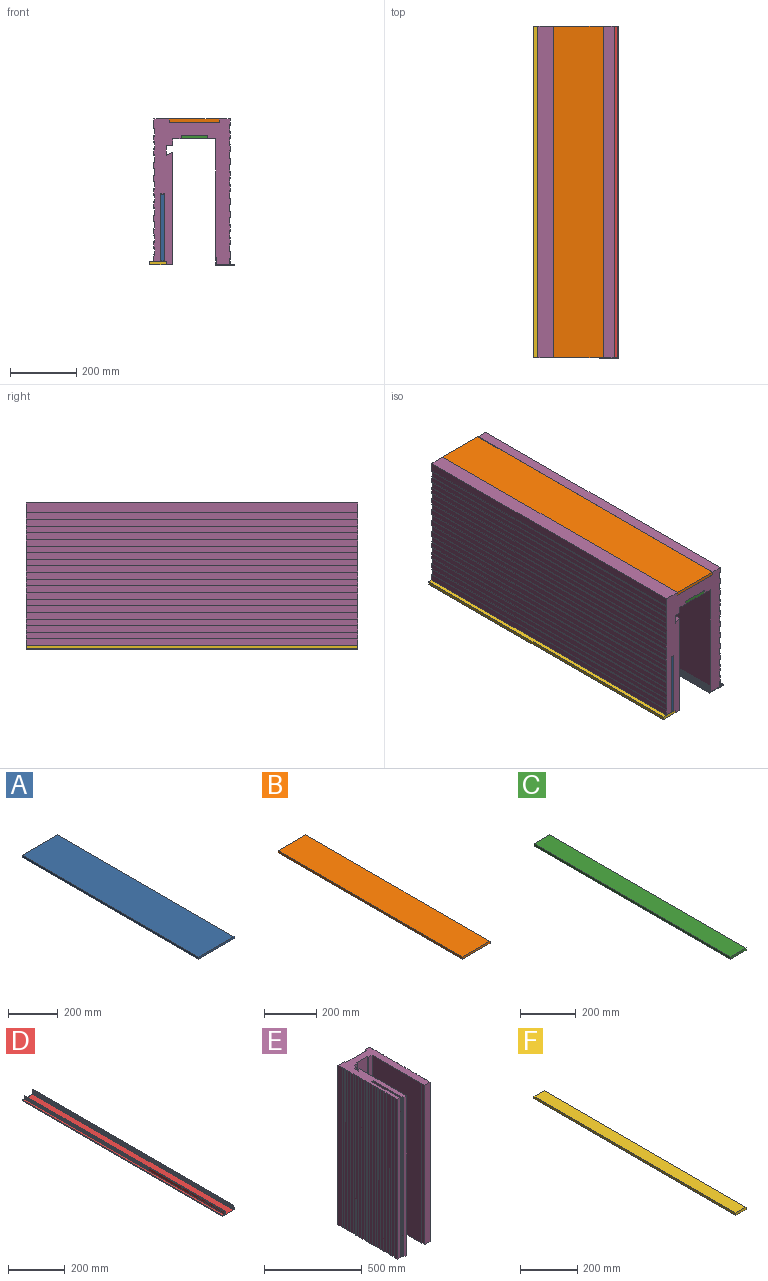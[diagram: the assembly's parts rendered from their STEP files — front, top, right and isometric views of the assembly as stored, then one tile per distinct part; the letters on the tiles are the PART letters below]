
ASSEMBLY  parts=6 mates=5
PART A: 6 faces, bbox 200x1000x10 mm
  f0: plane 1000x10mm, normal (-1,0,0), area 10000mm2, adj f1,f3,f4,f5
  f1: plane 1000x200mm, normal (0,0,-1), area 200000mm2, adj f0,f2,f4,f5
  f2: plane 1000x10mm, normal (1,0,0), area 10000mm2, adj f1,f3,f4,f5
  f3: plane 1000x200mm, normal (0,0,1), area 200000mm2, adj f0,f2,f4,f5
  f4: plane 200x10mm, normal (0,-1,0), area 2000mm2, adj f0,f1,f2,f3
  f5: plane 200x10mm, normal (0,1,0), area 2000mm2, adj f0,f1,f2,f3
PART B: 6 faces, bbox 150x1000x10 mm
  f0: plane 1000x10mm, normal (-1,0,0), area 10000mm2, adj f1,f3,f4,f5
  f1: plane 1000x150mm, normal (0,0,-1), area 150000mm2, adj f0,f2,f4,f5
  f2: plane 1000x10mm, normal (1,0,0), area 10000mm2, adj f1,f3,f4,f5
  f3: plane 1000x150mm, normal (0,0,1), area 150000mm2, adj f0,f2,f4,f5
  f4: plane 150x10mm, normal (0,-1,0), area 1500mm2, adj f0,f1,f2,f3
  f5: plane 150x10mm, normal (0,1,0), area 1500mm2, adj f0,f1,f2,f3
PART C: 6 faces, bbox 80x1000x10 mm
  f0: plane 1000x10mm, normal (-1,0,0), area 10000mm2, adj f1,f3,f4,f5
  f1: plane 1000x80mm, normal (0,0,-1), area 80000mm2, adj f0,f2,f4,f5
  f2: plane 1000x10mm, normal (1,0,0), area 10000mm2, adj f1,f3,f4,f5
  f3: plane 1000x80mm, normal (0,0,1), area 80000mm2, adj f0,f2,f4,f5
  f4: plane 80x10mm, normal (0,-1,0), area 800mm2, adj f0,f1,f2,f3
  f5: plane 80x10mm, normal (0,1,0), area 800mm2, adj f0,f1,f2,f3
PART D: 62 faces, bbox 57.5x1000x21 mm
  f0: plane 1000x14.3mm, normal (-1,0,0), area 14303.9mm2, adj f1,f2,f60,f61
  f1: plane 57.5x21mm, normal (0,-1,0), area 145.8mm2, adj f0,f2,f3,f4,f5,f6,f7,f8
  f2: plane 1000x11mm, normal (0,0,1), area 11000mm2, adj f0,f1,f3,f60
  f3: plane 1000x1.5mm, normal (1,0,0), area 1500mm2, adj f1,f2,f4,f60
  f4: plane 1000x1.5mm, normal (0,0,1), area 1500mm2, adj f1,f3,f5,f60
  f5: plane 1000x3mm, normal (-1,0,0), area 3000mm2, adj f1,f4,f6,f60
  f6: plane 1000x57.5mm, normal (0,0,-1), area 57500mm2, adj f1,f5,f7,f60
  f7: plane 1000x4mm, normal (1,0,0), area 4000mm2, adj f1,f6,f8,f60
  f8: plane 1000x1mm, normal (0,0,1), area 1000mm2, adj f1,f7,f9,f60
  f9: plane 1000x3mm, normal (-1,0,0), area 3000mm2, adj f1,f8,f10,f60
  f10: plane 1000x1mm, normal (0,0,1), area 1000mm2, adj f1,f9,f11,f60
  f11: plane 1000x7mm, normal (1,0,0), area 7000mm2, adj f1,f10,f12,f60
  f12: plane 1000x1mm, normal (0,0,-1), area 1000mm2, adj f1,f11,f13,f60
  f13: plane 1000x3mm, normal (-1,0,0), area 3000mm2, adj f1,f12,f14,f60
  f14: plane 1000x1mm, normal (0,0,-1), area 1000mm2, adj f1,f13,f15,f60
  f15: plane 1000x4mm, normal (1,0,0), area 4000mm2, adj f1,f14,f16,f60
  f16: plane 1000x2mm, normal (0,0,1), area 2000mm2, adj f1,f15,f17,f60
  f17: plane 1000x12mm, normal (1,0,0), area 12000mm2, adj f1,f16,f18,f60
  f18: plane 1000x1mm, normal (0,0,1), area 1000mm2, adj f1,f17,f19,f60
  f19: plane 1000x1.73mm, normal (-0.87,0,0.5), area 2000mm2, adj f1,f18,f20,f60
  f20: plane 1000x1mm, normal (0,0,-1), area 1000mm2, adj f1,f19,f21,f60
  f21: plane 1000x1.73mm, normal (-0.87,0,0.5), area 2000mm2, adj f1,f20,f22,f60
  f22: plane 1000x1mm, normal (0,0,-1), area 1000mm2, adj f1,f21,f23,f60
  f23: plane 1000x1.73mm, normal (-0.87,0,0.5), area 2000mm2, adj f1,f22,f24,f60
  f24: plane 1000x1mm, normal (0,0,-1), area 1000mm2, adj f1,f23,f25,f60
  f25: plane 1000x1.73mm, normal (-0.87,0,0.5), area 2000mm2, adj f1,f24,f26,f60
  f26: plane 1000x1mm, normal (0,0,-1), area 1000mm2, adj f1,f25,f27,f60
  f27: plane 1000x1.73mm, normal (-0.87,0,0.5), area 2000mm2, adj f1,f26,f28,f60
  f28: plane 1000x1mm, normal (0,0,-1), area 1000mm2, adj f1,f27,f29,f60
  f29: plane 1000x1.73mm, normal (-0.87,0,0.5), area 2000mm2, adj f1,f28,f30,f60
  f30: plane 1000x1mm, normal (0,0,-1), area 1000mm2, adj f1,f29,f31,f60
  f31: plane 1000x1.73mm, normal (-0.87,0,0.5), area 2000mm2, adj f1,f30,f32,f60
  f32: plane 1000x1mm, normal (0,0,-1), area 1000mm2, adj f1,f31,f33,f60
  f33: plane 1000x1.73mm, normal (-0.87,0,0.5), area 2000mm2, adj f1,f32,f34,f60
  f34: plane 1000x1mm, normal (0,0,-1), area 1000mm2, adj f1,f33,f35,f60
  f35: plane 1000x1.73mm, normal (-0.87,0,0.5), area 2000mm2, adj f1,f34,f36,f60
  f36: plane 1000x1mm, normal (0,0,-1), area 1000mm2, adj f1,f35,f37,f60
  f37: plane 1000x1.73mm, normal (-0.87,0,0.5), area 2000mm2, adj f1,f36,f38,f60
  f38: plane 1000x1mm, normal (0,0,-1), area 1000mm2, adj f1,f37,f39,f60
  f39: plane 1000x1.73mm, normal (-0.87,0,0.5), area 2000mm2, adj f1,f38,f40,f60
  f40: plane 1000x1mm, normal (0,0,-1), area 1000mm2, adj f1,f39,f41,f60
  f41: plane 1000x0.45mm, normal (-1,0,0), area 447.4mm2, adj f1,f40,f42,f60
  f42: plane 1000x41mm, normal (0,0,1), area 41000mm2, adj f1,f41,f43,f60
  f43: plane 1000x0.45mm, normal (1,0,0), area 447.4mm2, adj f1,f42,f44,f60
  f44: plane 1000x1mm, normal (0,0,-1), area 1000mm2, adj f1,f43,f45,f60
  f45: plane 1000x1.73mm, normal (0.87,0,0.5), area 2000mm2, adj f1,f44,f46,f60
  f46: plane 1000x1mm, normal (0,0,-1), area 1000mm2, adj f1,f45,f47,f60
  f47: plane 1000x1.73mm, normal (0.87,0,0.5), area 2000mm2, adj f1,f46,f48,f60
  f48: plane 1000x1mm, normal (0,0,-1), area 1000mm2, adj f1,f47,f49,f60
  f49: plane 1000x1.73mm, normal (0.87,0,0.5), area 2000mm2, adj f1,f48,f50,f60
  f50: plane 1000x1mm, normal (0,0,-1), area 1000mm2, adj f1,f49,f51,f60
  f51: plane 1000x1.73mm, normal (0.87,0,0.5), area 2000mm2, adj f1,f50,f52,f60
  f52: plane 1000x1mm, normal (0,0,-1), area 1000mm2, adj f1,f51,f53,f60
  f53: plane 1000x1.73mm, normal (0.87,0,0.5), area 2000mm2, adj f1,f52,f54,f60
  f54: plane 1000x1mm, normal (0,0,-1), area 1000mm2, adj f1,f53,f55,f60
  f55: plane 1000x1.73mm, normal (0.87,0,0.5), area 2000mm2, adj f1,f54,f56,f60
  f56: plane 1000x1mm, normal (0,0,-1), area 1000mm2, adj f1,f55,f57,f60
  f57: plane 1000x1.73mm, normal (0.87,0,0.5), area 2000mm2, adj f1,f56,f58,f60
  f58: plane 1000x1mm, normal (0,0,-1), area 1000mm2, adj f1,f57,f59,f60
  f59: plane 1000x1.73mm, normal (0.87,0,0.5), area 2000mm2, adj f1,f58,f60,f61
  f60: plane 57.5x21mm, normal (0,1,0), area 145.8mm2, adj f0,f2,f3,f4,f5,f6,f7,f8
  f61: plane 1000x1mm, normal (0,0,1), area 1000mm2, adj f0,f1,f59,f60
PART E: 112 faces, bbox 230x440x1000 mm
  f0: plane 1000x20mm, normal (-1,0,0), area 20000mm2, adj f50,f51,f106,f110
  f1: plane 1000x20mm, normal (-1,0,0), area 20000mm2, adj f50,f51,f103,f107
  f2: plane 1000x20mm, normal (-1,0,0), area 20000mm2, adj f50,f51,f100,f104
  f3: plane 1000x20mm, normal (-1,0,0), area 20000mm2, adj f50,f51,f97,f101
  f4: plane 1000x20mm, normal (-1,0,0), area 20000mm2, adj f50,f51,f94,f98
  f5: plane 1000x20mm, normal (-1,0,0), area 20000mm2, adj f50,f51,f91,f95
  f6: plane 1000x20mm, normal (-1,0,0), area 20000mm2, adj f50,f51,f88,f92
  f7: plane 1000x20mm, normal (-1,0,0), area 20000mm2, adj f50,f51,f85,f89
  f8: plane 1000x20mm, normal (-1,0,0), area 20000mm2, adj f50,f51,f82,f86
  f9: plane 1000x30mm, normal (-1,0,0), area 30000mm2, adj f21,f50,f51,f83
  f10: plane 1000x22mm, normal (1,0,0), area 22000mm2, adj f45,f50,f51,f79
  f11: plane 1000x20mm, normal (1,0,0), area 20000mm2, adj f50,f51,f76,f80
  f12: plane 1000x20mm, normal (1,0,0), area 20000mm2, adj f50,f51,f73,f77
  f13: plane 1000x20mm, normal (1,0,0), area 20000mm2, adj f50,f51,f70,f74
  f14: plane 1000x20mm, normal (1,0,0), area 20000mm2, adj f50,f51,f67,f71
  f15: plane 1000x20mm, normal (1,0,0), area 20000mm2, adj f50,f51,f64,f68
  f16: plane 1000x20mm, normal (1,0,0), area 20000mm2, adj f50,f51,f61,f65
  f17: plane 1000x20mm, normal (1,0,0), area 20000mm2, adj f50,f51,f58,f62
  f18: plane 1000x20mm, normal (1,0,0), area 20000mm2, adj f50,f51,f55,f59
  f19: plane 1000x20mm, normal (1,0,0), area 20000mm2, adj f50,f51,f52,f56
  f20: plane 1000x10mm, normal (1,0,0), area 10000mm2, adj f21,f49,f50,f51
  f21: plane 1000x46.75mm, normal (0,1,0), area 46750mm2, adj f9,f20,f50,f51
  f22: plane 1000x20mm, normal (-1,0,0), area 20000mm2, adj f23,f50,f51,f109
  f23: plane 1000x20.5mm, normal (0,-1,0), area 20500mm2, adj f22,f24,f50,f51
  f24: plane 1000x205mm, normal (1,0,0), area 205000mm2, adj f23,f25,f50,f51
  f25: cylinder r=10mm len=1000mm, axis (0,0,-1), area 11054.3mm2, adj f24,f26,f50,f51
  f26: plane 1000x205mm, normal (-1,0,0), area 205000mm2, adj f25,f27,f50,f51
  f27: plane 1000x6mm, normal (0,-1,0), area 6000mm2, adj f26,f28,f50,f51
  f28: plane 1000x10mm, normal (-1,0,0), area 10000mm2, adj f27,f29,f50,f51
  f29: plane 1000x20mm, normal (0,-1,0), area 20000mm2, adj f28,f30,f50,f51
  f30: plane 1000x340.19mm, normal (1,0,0), area 340190.5mm2, adj f29,f31,f50,f51
  f31: plane 1000x20mm, normal (-0.45,0.89,0), area 22446.5mm2, adj f30,f32,f50,f51
  f32: plane 1000x30mm, normal (1,0,0), area 30000mm2, adj f31,f33,f50,f51
  f33: plane 1000x20mm, normal (0,-1,0), area 20000mm2, adj f32,f34,f50,f51
  f34: plane 1000x20mm, normal (1,0,0), area 20000mm2, adj f33,f35,f50,f51
  f35: plane 1000x24.75mm, normal (0,-1,0), area 24750mm2, adj f34,f36,f50,f51
  f36: plane 1000x10mm, normal (1,0,0), area 10000mm2, adj f35,f37,f50,f51
  f37: plane 1000x80.5mm, normal (0,-1,0), area 80500mm2, adj f36,f38,f50,f51
  f38: plane 1000x10mm, normal (-1,0,0), area 10000mm2, adj f37,f39,f50,f51
  f39: plane 1000x24.75mm, normal (0,-1,0), area 24750mm2, adj f38,f40,f50,f51
  f40: plane 1000x357.5mm, normal (-1,0,0), area 357500mm2, adj f39,f41,f50,f51
  f41: plane 1000x2mm, normal (0,-1,0), area 2000mm2, adj f40,f42,f50,f51
  f42: plane 1000x21.5mm, normal (-1,0,0), area 21500mm2, adj f41,f43,f50,f51
  f43: plane 1000x39.1mm, normal (0,-1,0), area 39100mm2, adj f42,f44,f50,f51
  f44: plane 1000x18.5mm, normal (1,0,0), area 18500mm2, adj f43,f45,f50,f51
  f45: plane 1000x1.9mm, normal (0,-1,0), area 1900mm2, adj f10,f44,f50,f51
  f46: plane 1000x18.5mm, normal (1,0,0), area 18500mm2, adj f47,f50,f51,f53
  f47: plane 1000x32.75mm, normal (0,1,0), area 32750mm2, adj f46,f48,f50,f51
  f48: plane 1000x10mm, normal (-1,0,0), area 10000mm2, adj f47,f49,f50,f51
  f49: plane 1000x150.5mm, normal (0,1,0), area 150500mm2, adj f20,f48,f50,f51
  f50: plane 440x230mm, normal (0,0,1), area 45478.8mm2, adj f0,f1,f2,f3,f4,f5,f6,f7
  f51: plane 440x230mm, normal (0,0,-1), area 45478.8mm2, adj f0,f1,f2,f3,f4,f5,f6,f7
  f52: plane 1000x2mm, normal (-0.71,0.71,0), area 2828.4mm2, adj f19,f50,f51,f54
  f53: plane 1000x2mm, normal (-0.71,-0.71,0), area 2828.4mm2, adj f46,f50,f51,f54
  f54: plane 1000x24mm, normal (1,0,0), area 24000mm2, adj f50,f51,f52,f53
  f55: plane 1000x2mm, normal (-0.71,0.71,0), area 2828.4mm2, adj f18,f50,f51,f57
  f56: plane 1000x2mm, normal (-0.71,-0.71,0), area 2828.4mm2, adj f19,f50,f51,f57
  f57: plane 1000x24mm, normal (1,0,0), area 24000mm2, adj f50,f51,f55,f56
  f58: plane 1000x2mm, normal (-0.71,0.71,0), area 2828.4mm2, adj f17,f50,f51,f60
  f59: plane 1000x2mm, normal (-0.71,-0.71,0), area 2828.4mm2, adj f18,f50,f51,f60
  f60: plane 1000x24mm, normal (1,0,0), area 24000mm2, adj f50,f51,f58,f59
  f61: plane 1000x2mm, normal (-0.71,0.71,0), area 2828.4mm2, adj f16,f50,f51,f63
  f62: plane 1000x2mm, normal (-0.71,-0.71,0), area 2828.4mm2, adj f17,f50,f51,f63
  f63: plane 1000x24mm, normal (1,0,0), area 24000mm2, adj f50,f51,f61,f62
  f64: plane 1000x2mm, normal (-0.71,0.71,0), area 2828.4mm2, adj f15,f50,f51,f66
  f65: plane 1000x2mm, normal (-0.71,-0.71,0), area 2828.4mm2, adj f16,f50,f51,f66
  f66: plane 1000x24mm, normal (1,0,0), area 24000mm2, adj f50,f51,f64,f65
  f67: plane 1000x2mm, normal (-0.71,0.71,0), area 2828.4mm2, adj f14,f50,f51,f69
  f68: plane 1000x2mm, normal (-0.71,-0.71,0), area 2828.4mm2, adj f15,f50,f51,f69
  f69: plane 1000x24mm, normal (1,0,0), area 24000mm2, adj f50,f51,f67,f68
  f70: plane 1000x2mm, normal (-0.71,0.71,0), area 2828.4mm2, adj f13,f50,f51,f72
  f71: plane 1000x2mm, normal (-0.71,-0.71,0), area 2828.4mm2, adj f14,f50,f51,f72
  f72: plane 1000x24mm, normal (1,0,0), area 24000mm2, adj f50,f51,f70,f71
  f73: plane 1000x2mm, normal (-0.71,0.71,0), area 2828.4mm2, adj f12,f50,f51,f75
  f74: plane 1000x2mm, normal (-0.71,-0.71,0), area 2828.4mm2, adj f13,f50,f51,f75
  f75: plane 1000x24mm, normal (1,0,0), area 24000mm2, adj f50,f51,f73,f74
  f76: plane 1000x2mm, normal (-0.71,0.71,0), area 2828.4mm2, adj f11,f50,f51,f78
  f77: plane 1000x2mm, normal (-0.71,-0.71,0), area 2828.4mm2, adj f12,f50,f51,f78
  f78: plane 1000x24mm, normal (1,0,0), area 24000mm2, adj f50,f51,f76,f77
  f79: plane 1000x2mm, normal (-0.71,0.71,0), area 2828.4mm2, adj f10,f50,f51,f81
  f80: plane 1000x2mm, normal (-0.71,-0.71,0), area 2828.4mm2, adj f11,f50,f51,f81
  f81: plane 1000x24mm, normal (1,0,0), area 24000mm2, adj f50,f51,f79,f80
  f82: plane 1000x2mm, normal (0.71,0.71,0), area 2828.4mm2, adj f8,f50,f51,f84
  f83: plane 1000x2mm, normal (0.71,-0.71,0), area 2828.4mm2, adj f9,f50,f51,f84
  f84: plane 1000x24mm, normal (-1,0,0), area 24000mm2, adj f50,f51,f82,f83
  f85: plane 1000x2mm, normal (0.71,0.71,0), area 2828.4mm2, adj f7,f50,f51,f87
  f86: plane 1000x2mm, normal (0.71,-0.71,0), area 2828.4mm2, adj f8,f50,f51,f87
  f87: plane 1000x24mm, normal (-1,0,0), area 24000mm2, adj f50,f51,f85,f86
  f88: plane 1000x2mm, normal (0.71,0.71,0), area 2828.4mm2, adj f6,f50,f51,f90
  f89: plane 1000x2mm, normal (0.71,-0.71,0), area 2828.4mm2, adj f7,f50,f51,f90
  f90: plane 1000x24mm, normal (-1,0,0), area 24000mm2, adj f50,f51,f88,f89
  f91: plane 1000x2mm, normal (0.71,0.71,0), area 2828.4mm2, adj f5,f50,f51,f93
  f92: plane 1000x2mm, normal (0.71,-0.71,0), area 2828.4mm2, adj f6,f50,f51,f93
  f93: plane 1000x24mm, normal (-1,0,0), area 24000mm2, adj f50,f51,f91,f92
  f94: plane 1000x2mm, normal (0.71,0.71,0), area 2828.4mm2, adj f4,f50,f51,f96
  f95: plane 1000x2mm, normal (0.71,-0.71,0), area 2828.4mm2, adj f5,f50,f51,f96
  f96: plane 1000x24mm, normal (-1,0,0), area 24000mm2, adj f50,f51,f94,f95
  f97: plane 1000x2mm, normal (0.71,0.71,0), area 2828.4mm2, adj f3,f50,f51,f99
  f98: plane 1000x2mm, normal (0.71,-0.71,0), area 2828.4mm2, adj f4,f50,f51,f99
  f99: plane 1000x24mm, normal (-1,0,0), area 24000mm2, adj f50,f51,f97,f98
  f100: plane 1000x2mm, normal (0.71,0.71,0), area 2828.4mm2, adj f2,f50,f51,f102
  f101: plane 1000x2mm, normal (0.71,-0.71,0), area 2828.4mm2, adj f3,f50,f51,f102
  f102: plane 1000x24mm, normal (-1,0,0), area 24000mm2, adj f50,f51,f100,f101
  f103: plane 1000x2mm, normal (0.71,0.71,0), area 2828.4mm2, adj f1,f50,f51,f105
  f104: plane 1000x2mm, normal (0.71,-0.71,0), area 2828.4mm2, adj f2,f50,f51,f105
  f105: plane 1000x24mm, normal (-1,0,0), area 24000mm2, adj f50,f51,f103,f104
  f106: plane 1000x2mm, normal (0.71,0.71,0), area 2828.4mm2, adj f0,f50,f51,f108
  f107: plane 1000x2mm, normal (0.71,-0.71,0), area 2828.4mm2, adj f1,f50,f51,f108
  f108: plane 1000x24mm, normal (-1,0,0), area 24000mm2, adj f50,f51,f106,f107
  f109: plane 1000x2mm, normal (0.71,0.71,0), area 2828.4mm2, adj f22,f50,f51,f111
  f110: plane 1000x2mm, normal (0.71,-0.71,0), area 2828.4mm2, adj f0,f50,f51,f111
  f111: plane 1000x24mm, normal (-1,0,0), area 24000mm2, adj f50,f51,f109,f110
PART F: 6 faces, bbox 50x1000x10 mm
  f0: plane 1000x10mm, normal (-1,0,0), area 10000mm2, adj f1,f3,f4,f5
  f1: plane 1000x50mm, normal (0,0,-1), area 50000mm2, adj f0,f2,f4,f5
  f2: plane 1000x10mm, normal (1,0,0), area 10000mm2, adj f1,f3,f4,f5
  f3: plane 1000x50mm, normal (0,0,1), area 50000mm2, adj f0,f2,f4,f5
  f4: plane 50x10mm, normal (0,-1,0), area 500mm2, adj f0,f1,f2,f3
  f5: plane 50x10mm, normal (0,1,0), area 500mm2, adj f0,f1,f2,f3
PLACE A rot(axis=(0,1,0),90deg) t=(-216.83,500,-161.72)mm
PLACE B t=(-190.83,500,55.28)mm fixed
PLACE C t=(-155.83,500,5.28)mm
PLACE D rot(axis=(0,0,1),180deg) t=(-52.58,-500,-375.22)mm
PLACE E rot(axis=(1,0,0),90deg) t=(-169.34,500,-104.89)mm
PLACE F t=(-250.58,500,-374.72)mm
MATE fastened A.f4 <-> E.f50  axis (0,-1,0) through (-206.58,-500,-159.72)mm
MATE fastened E.f50 <-> B.f4  axis (0,-1,0) through (-190.83,-500,65.28)mm
MATE fastened C.f4 <-> E.f50  axis (0,-1,0) through (-155.83,-500,15.28)mm
MATE fastened D.f60 <-> E.f50  axis (0,-1,0) through (-48.58,-500,-373.72)mm
MATE fastened F.f4 <-> E.f50  axis (0,-1,0) through (-200.58,-500,-364.72)mm
